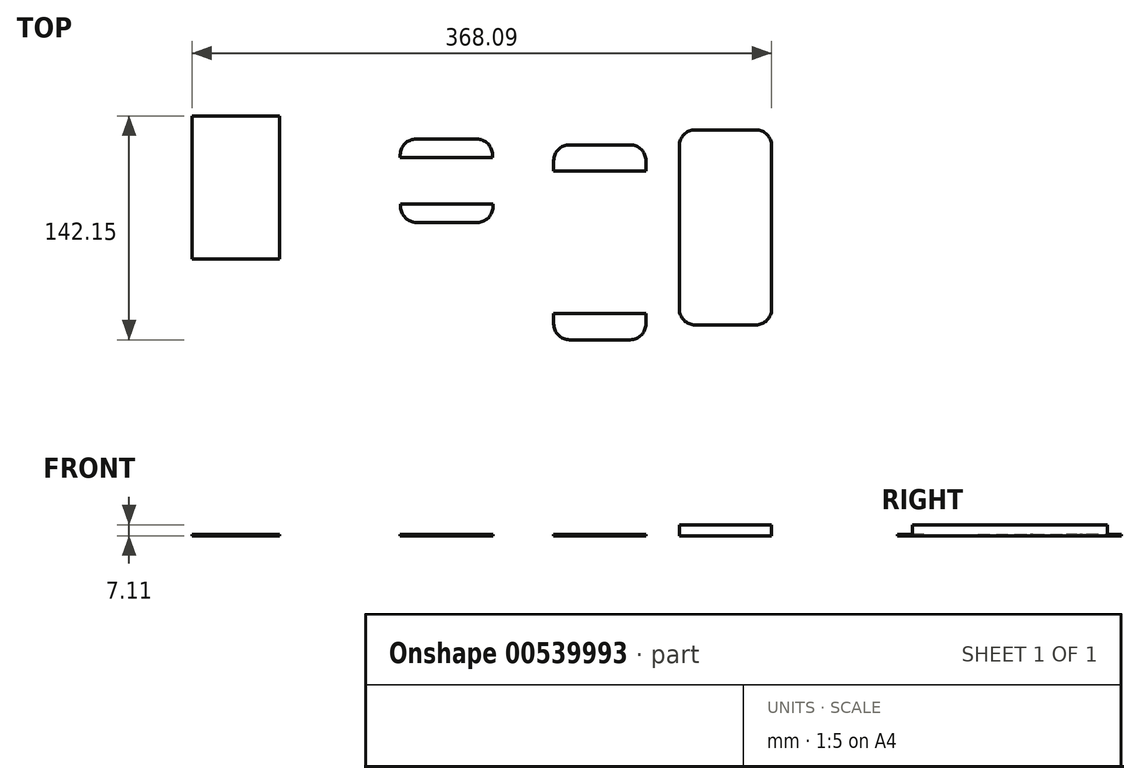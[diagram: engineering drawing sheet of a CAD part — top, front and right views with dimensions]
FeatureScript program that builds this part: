
annotation { "Feature Type Name" : "Feature", "Feature Type Description" : "" }
export const myFeature = defineFeature(function(context is Context, id is Id, definition is map)
    precondition{}
    {
        {
            var Q0;
            Q0=qCreatedBy(makeId("Top.planeOp"),FACE);
            var sketch = newSketch(context, id + "F0", { "sketchPlane" : qUnion([Q0])});
            skLineSegment(sketch, "E0.bottom", {"start": v(29.29, -61.91) * mm, "end": v(-29.28, -61.91) * mm});
            skLineSegment(sketch, "E0.top", {"start": v(29.28, 61.91) * mm, "end": v(-29.29, 61.91) * mm});
            skLineSegment(sketch, "E0.left", {"start": v(29.29, -61.91) * mm, "end": v(29.28, 61.92) * mm});
            skLineSegment(sketch, "E0.right", {"start": v(-29.28, -61.91) * mm, "end": v(-29.29, 61.92) * mm});
            skPoint(sketch, "E0.middle", {"position": v(0, 0) * mm});
            skSolve(sketch);
        }
        {
            var Q0;
            Q0=makeQuery(id+"F0.imprint","IMPRINT",FACE,{"disambiguationData":[TD([[makeQuery(id+"F0.imprint","IMPRINT",EDGE,{"derivedFrom":sQuery(id+"F0.wireOp",EDGE,"E0.bottom")}),-1.0]])]});
            extrude(context, id + "F1", {"entities" : qUnion([Q0]), "depth" : 7.11 * mm, "offsetDistance" : 25 * mm});
        }
        {
            var Q0;
            Q0=makeQuery(id+"F1.opExtrude","SWEPT_EDGE",EDGE,{"disambiguationData":[OSD([sQuery(id+"F0.wireOp",EDGE,"E0.bottom"),sQuery(id+"F0.wireOp",EDGE,"E0.left")])]});
            var Q1;
            Q1=makeQuery(id+"F1.opExtrude","SWEPT_EDGE",EDGE,{"disambiguationData":[OSD([sQuery(id+"F0.wireOp",EDGE,"E0.bottom"),sQuery(id+"F0.wireOp",EDGE,"E0.right")])]});
            var Q2;
            Q2=makeQuery(id+"F1.opExtrude","SWEPT_EDGE",EDGE,{"disambiguationData":[OSD([sQuery(id+"F0.wireOp",EDGE,"E0.top"),sQuery(id+"F0.wireOp",EDGE,"E0.left")])]});
            var Q3;
            Q3=makeQuery(id+"F1.opExtrude","SWEPT_EDGE",EDGE,{"disambiguationData":[OSD([sQuery(id+"F0.wireOp",EDGE,"E0.top"),sQuery(id+"F0.wireOp",EDGE,"E0.right")])]});
            fillet(context, id + "F2", {"entities" : qUnion([Q0, Q1, Q2, Q3]), "radius" : 10 * mm, "tangentPropagation" : true, "allowEdgeOverflow" : false});
        }
        {
            var Q0;
            Q0=qCreatedBy(makeId("Top.planeOp"),FACE);
            var sketch = newSketch(context, id + "F3", { "sketchPlane" : qUnion([Q0])});
            skLineSegment(sketch, "E1.bottom", {"start": v(-109.1, 52.45) * mm, "end": v(-50.54, 52.45) * mm});
            skLineSegment(sketch, "E1.top", {"start": v(-109.1, 35.73) * mm, "end": v(-50.54, 35.73) * mm});
            skLineSegment(sketch, "E1.left", {"start": v(-109.1, 52.45) * mm, "end": v(-109.1, 35.73) * mm});
            skLineSegment(sketch, "E1.right", {"start": v(-50.54, 52.45) * mm, "end": v(-50.54, 35.73) * mm});
            skLineSegment(sketch, "E2.bottom", {"start": v(-50.54, 35.73) * mm, "end": v(-51.98, 35.73) * mm});
            skLineSegment(sketch, "E2.top", {"start": v(-50.54, -54.66) * mm, "end": v(-51.98, -54.66) * mm});
            skLineSegment(sketch, "E2.left", {"start": v(-50.54, 35.73) * mm, "end": v(-50.54, -54.66) * mm});
            skLineSegment(sketch, "E2.right", {"start": v(-51.98, 35.73) * mm, "end": v(-51.98, -54.66) * mm});
            skLineSegment(sketch, "E3.bottom", {"start": v(-109.1, 35.73) * mm, "end": v(-107.67, 35.73) * mm});
            skLineSegment(sketch, "E3.top", {"start": v(-109.1, -54.66) * mm, "end": v(-107.67, -54.66) * mm});
            skLineSegment(sketch, "E3.left", {"start": v(-109.1, 35.73) * mm, "end": v(-109.1, -54.66) * mm});
            skLineSegment(sketch, "E3.right", {"start": v(-107.67, 35.73) * mm, "end": v(-107.67, -54.66) * mm});
            skLineSegment(sketch, "E4.bottom", {"start": v(-109.1, -54.66) * mm, "end": v(-50.54, -54.66) * mm});
            skLineSegment(sketch, "E4.top", {"start": v(-109.1, -71.38) * mm, "end": v(-50.54, -71.38) * mm});
            skLineSegment(sketch, "E4.left", {"start": v(-109.1, -54.66) * mm, "end": v(-109.1, -71.38) * mm});
            skLineSegment(sketch, "E4.right", {"start": v(-50.54, -54.66) * mm, "end": v(-50.54, -71.38) * mm});
            skSolve(sketch);
        }
        {
            var Q0;
            Q0=makeQuery(id+"F3.imprint","IMPRINT",FACE,{"disambiguationData":[TD([[makeQuery(id+"F3.imprint","IMPRINT",EDGE,{"derivedFrom":sQuery(id+"F3.wireOp",EDGE,"E1.bottom")}),-1.0]])]});
            var Q1;
            Q1=makeQuery(id+"F3.imprint","IMPRINT",FACE,{"disambiguationData":[TD([[makeQuery(id+"F3.imprint","IMPRINT",EDGE,{"derivedFrom":sQuery(id+"F3.wireOp",EDGE,"E3.bottom")}),-1.0]])]});
            var Q2;
            Q2=makeQuery(id+"F3.imprint","IMPRINT",FACE,{"disambiguationData":[TD([[makeQuery(id+"F3.imprint","IMPRINT",EDGE,{"derivedFrom":sQuery(id+"F3.wireOp",EDGE,"E2.bottom")}),1.0]])]});
            var Q3;
            Q3=makeQuery(id+"F3.imprint","IMPRINT",FACE,{"disambiguationData":[TD([[makeQuery(id+"F3.imprint","IMPRINT",EDGE,{"derivedFrom":sQuery(id+"F3.wireOp",EDGE,"E4.top")}),1.0]])]});
            extrude(context, id + "F4", {"entities" : qUnion([Q0, Q1, Q2, Q3]), "depth" : 1 * mm, "offsetDistance" : 25 * mm});
        }
        {
            var Q0;
            Q0=makeQuery(id+"F4.opExtrude","SWEPT_EDGE",EDGE,{"disambiguationData":[OSD([sQuery(id+"F3.wireOp",EDGE,"E1.bottom"),sQuery(id+"F3.wireOp",EDGE,"E1.left")])]});
            var Q1;
            Q1=makeQuery(id+"F4.opExtrude","SWEPT_EDGE",EDGE,{"disambiguationData":[OSD([sQuery(id+"F3.wireOp",EDGE,"E4.top"),sQuery(id+"F3.wireOp",EDGE,"E4.left")])]});
            var Q2;
            Q2=makeQuery(id+"F4.opExtrude","SWEPT_EDGE",EDGE,{"disambiguationData":[OSD([sQuery(id+"F3.wireOp",EDGE,"E4.top"),sQuery(id+"F3.wireOp",EDGE,"E4.right")])]});
            var Q3;
            Q3=makeQuery(id+"F4.opExtrude","SWEPT_EDGE",EDGE,{"disambiguationData":[OSD([sQuery(id+"F3.wireOp",EDGE,"E1.bottom"),sQuery(id+"F3.wireOp",EDGE,"E1.right")])]});
            fillet(context, id + "F5", {"entities" : qUnion([Q0, Q1, Q2, Q3]), "radius" : 10 * mm, "tangentPropagation" : true, "allowEdgeOverflow" : false});
        }
        {
            var Q0;
            Q0=qCreatedBy(makeId("Top.planeOp"),FACE);
            var sketch = newSketch(context, id + "F6", { "sketchPlane" : qUnion([Q0])});
            skLineSegment(sketch, "E5.bottom", {"start": v(-206.58, 56.09) * mm, "end": v(-148, 56.09) * mm});
            skLineSegment(sketch, "E5.top", {"start": v(-206.58, 44.49) * mm, "end": v(-148, 44.49) * mm});
            skLineSegment(sketch, "E5.left", {"start": v(-206.58, 56.09) * mm, "end": v(-206.58, 44.49) * mm});
            skLineSegment(sketch, "E5.right", {"start": v(-148, 56.09) * mm, "end": v(-148, 44.49) * mm});
            skLineSegment(sketch, "E6.bottom", {"start": v(-206.28, 14.73) * mm, "end": v(-147.7, 14.73) * mm});
            skLineSegment(sketch, "E6.top", {"start": v(-206.28, 3.13) * mm, "end": v(-147.7, 3.13) * mm});
            skLineSegment(sketch, "E6.left", {"start": v(-206.28, 14.73) * mm, "end": v(-206.28, 3.13) * mm});
            skLineSegment(sketch, "E6.right", {"start": v(-147.7, 14.73) * mm, "end": v(-147.7, 3.13) * mm});
            skSolve(sketch);
        }
        {
            var Q0;
            Q0 = qSketchRegion(id + "F6", true);
            extrude(context, id + "F7", {"entities" : qUnion([Q0]), "depth" : 1 * mm, "offsetDistance" : 25 * mm});
        }
        {
            var Q0;
            Q0=makeQuery(id+"F7.opExtrude","SWEPT_EDGE",EDGE,{"disambiguationData":[OSD([sQuery(id+"F6.wireOp",EDGE,"E5.bottom"),sQuery(id+"F6.wireOp",EDGE,"E5.right")])]});
            var Q1;
            Q1=makeQuery(id+"F7.opExtrude","SWEPT_EDGE",EDGE,{"disambiguationData":[OSD([sQuery(id+"F6.wireOp",EDGE,"E5.bottom"),sQuery(id+"F6.wireOp",EDGE,"E5.left")])]});
            var Q2;
            Q2=makeQuery(id+"F7.opExtrude","SWEPT_EDGE",EDGE,{"disambiguationData":[OSD([sQuery(id+"F6.wireOp",EDGE,"E6.top"),sQuery(id+"F6.wireOp",EDGE,"E6.left")])]});
            var Q3;
            Q3=makeQuery(id+"F7.opExtrude","SWEPT_EDGE",EDGE,{"disambiguationData":[OSD([sQuery(id+"F6.wireOp",EDGE,"E6.top"),sQuery(id+"F6.wireOp",EDGE,"E6.right")])]});
            fillet(context, id + "F8", {"entities" : qUnion([Q0, Q1, Q2, Q3]), "radius" : 10 * mm, "tangentPropagation" : true, "allowEdgeOverflow" : false});
        }
        {
            var Q0;
            Q0=qCreatedBy(makeId("Top.planeOp"),FACE);
            var sketch = newSketch(context, id + "F9", { "sketchPlane" : qUnion([Q0])});
            skLineSegment(sketch, "E7.bottom", {"start": v(-283.1, -20.2) * mm, "end": v(-338.8, -20.2) * mm});
            skLineSegment(sketch, "E7.top", {"start": v(-283.1, 70.77) * mm, "end": v(-338.8, 70.77) * mm});
            skLineSegment(sketch, "E7.left", {"start": v(-283.1, -20.2) * mm, "end": v(-283.1, 70.77) * mm});
            skLineSegment(sketch, "E7.right", {"start": v(-338.8, -20.2) * mm, "end": v(-338.8, 70.77) * mm});
            skPoint(sketch, "E7.middle", {"position": v(-310.95, 25.29) * mm});
            skSolve(sketch);
        }
        {
            var Q0;
            Q0=makeQuery(id+"F9.imprint","IMPRINT",FACE,{"disambiguationData":[TD([[makeQuery(id+"F9.imprint","IMPRINT",EDGE,{"derivedFrom":sQuery(id+"F9.wireOp",EDGE,"E7.bottom")}),-1.0]])]});
            extrude(context, id + "F10", {"entities" : qUnion([Q0]), "depth" : 1 * mm, "offsetDistance" : 25 * mm});
        }
    });
